# Revit family: IS_Iom_A9111_BIM_DE
name_source: partatom
category: Plumbing Fixtures
revit_build: Autodesk Revit MEP 2016 (Build: 20161004_0715(x64)
units: mm (PartAtom-declared; Revit-internal decimal feet)

## family parameters
Always vertical = No
Cut with Voids When Loaded = No
OmniClass Number = 23.45.05.14.21.11
OmniClass Title = Bath/Shower Units
Part Type = Normal
Room Calculation Point = No
Round Connector Dimension = Use Diameter
Shared = No
Work Plane-Based = No

## types (1)
- A9111AA IOM cosmetic mirror
    Accessories = www.idealstandard.de\ersatzteile
    AssetType = Fixed
    BIMObjectName = ISI_IdealStandard_BathroomMirrors_Iom_A9111AA
    BIMobject category = Mirrors
    BOSUseNativeGeometries = 1
    BarCode = 4015413328005
    Brand = Ideal Standard
    Brand url = http://www.idealstandard.de
    CodePerformance = 0
    Color = Chrome
    ConnectionType = Plumbing
    Cost = 0 $
    CurrencyUnit = €
    CurrentRevision = 1
    Date of publishing = 20/12/2017
    Description = IS Kosmetikspiegel IOM Chrom
    DurationUnit = Year
    EAN code = https://4015413328005
    Edition number = 1
    ExpectedLife = 25
    Features = IS Kosmetikspiegel IOM Chrom
    Finish = Chrome
    IFC Classification = Sanitary Terminal
    IfcExportAs = IfcSanitaryTerminalType
    Installation instructions = http://www.idealstandard.de
    InstallationInstructions = www.idealstandard.de\produkte
    MainColor = Chrome
    MaintenanceInformation = www.idealstandard.de\produkte
    Manufacturer name = Ideal Standard
    ManufacturerURL = http://www.idealstandard.de
    Material = 0
    Material main = Glass
    Model = A9111AA
    ModelNumber = A9111AA
    ModelReference = IS Kosmetikspiegel IOM Chrom
    NBS Reference Code = 45-55-06
    NBS Reference Description = Bathroom Mirrors
    Name = BathroomMirrors_Iom_A9111AA
    NettWeight = 1.16 Kg
    Nominal height = 293
    Nominal width = 238
    NominalDepth = 41 mm  [stored 0.134514 ft]
    NominalHeight = 257 mm
    NominalLength = 41 mm  [stored 0.134514 ft]
    NominalWidth = 275 mm
    OmniClass Code = 23-31 25 00
    OmniClass Description = Toilet and Bath Specialties
    Product Guid = 07d0ed7c-8885-4bdc-91d6-0b782be3049f
    Product SKU = A9111
    Product data url = https://bimobject.com
    Product family = Sanitary
    Product group = Mirror
    Product name = IOM cosmetic mirror
    Product url = http://www.idealstandard.de
    ProductInformation = www.idealstandard.de/produkte
    QR code = http://bimobject.com
    Shape = Sculptured
    Size = 275x41x257 mm
    Space = Internal
    SpareParts = www.idealstandard.de/ersatzteile
    Technical description = http://www.idealstandard.de
    URL = http://www.idealstandard.de
    Uniclass 1.4 Code = L8732
    Uniclass 1.4 Description = Mirrors
    Uniclass 2.0 Code = PR-45-55-06
    Uniclass 2.0 Description = Bathroom Mirrors
    Uniclass 2015 Code = Pr_25_71_53_06
    Uniclass 2015 Name = Bathroom mirrors
    Uniclass2015Code = Pr_25_71_53_06
    Uniclass2015Title = Bathroom mirrors
    Uniclass2015Version = Products v1.1
    Version = 1
    VolumeUnits = Litres
    Weight Net (Kg) = 1.16

note: [stored X ft] marks values corroborated as IEEE doubles in the binary element streams (Revit-internal decimal feet)

## geometry (parser evidence)
native form markers: Blend x4, Sweep x1
no freeform markers — native parametric forms only
